# Revit family: 820-20-028-DN150-1600
name_source: partatom
category: Generic Models
units: mm (PartAtom-declared; Revit-internal decimal feet)

## family parameters
Always vertical = Yes
Can host rebar = No
Cut with Voids When Loaded = No
Part Type = Normal
Room Calculation Point = No
Round Connector Dimension = Use Diameter
Shared = No
Work Plane-Based = No

## types (33) — shared parameters
820-0150-20-041E0160002 = DN150_PN 10/16
820-0200-20-041E0030002 = DN200_PN10
820-0200-20-041E0160002 = DN200_PN16
820-0250-20-041E0030002 = DN250_PN10
820-0250-20-041E0160002 = DN250_PN16
820-0300-20-041E0030002 = DN300_PN10
820-0300-20-041E0160002 = DN300_PN16
820-0350-20-04010030002 = DN350_PN10
820-0350-20-04010160002 = DN350_PN16
820-0400-20-04010030002 = DN400_PN10
820-0400-20-04010160002 = DN400_PN16
820-0450-20-04040031002 = DN450_PN10
820-0450-20-04040161002 = DN450_PN16
820-0500-20-04040031002 = DN500_PN10
820-0500-20-04040161002 = DN500_PN16
820-0600-20-04040031002 = DN600_PN10
820-0600-20-04040161002 = DN600_PN16
820-0700-20-04040031002 = DN700_PN10
820-0700-20-04040161002 = DN700_PN16
820-0800-20-04040031002 = DN800_PN10
820-0800-20-04040161002 = DN800_PN16
820-0900-20-04040031002 = DN900_PN10
820-0900-20-04040161002 = DN900_PN16
820-1000-20-04040031002 = DN1000_PN10
820-1000-20-04040161002 = DN1000_PN16
820-1100-20-04040031002 = DN1100_PN10
820-1100-20-04040161002 = DN1100_PN16
820-1200-20-04040031002 = DN1200_PN10
820-1200-20-04040161002 = DN1200_PN16
820-1400-20-04040031002 = DN1400_PN10
820-1400-20-04040161002 = DN1400_PN16
820-1600-20-04040031002 = DN1600_PN10
820-1600-20-04040161002 = DN1600_PN16
Body_wallthickness = 10 mm  [stored 0.0328084 ft]
Description_ = AVK CENTRIC U-SECTION BUTTERFLY VALVE
Search_table = 820-20-028-DN150-1600
URL product pages = https://www.avkvalves.com

## per-type parameters (varying)
| type | DN | F | F2 | Flange_thickness | H2 | ID | L | L2 | L_ref | L_ref_2 | L_ref_3 | W2_ref |
| DN0150_PN10/16 | 150 mm | 14 mm  [stored 0.0459318 ft] | 16 mm  [stored 0.0524934 ft] | 10 mm  [stored 0.0328084 ft] | 143 mm | 75 mm | 56 mm  [stored 0.183727 ft] | 143 mm | 36 mm  [stored 0.11811 ft] | 54 mm  [stored 0.177165 ft] | 30 mm  [stored 0.0984252 ft] | 210 mm |
| DN0200_PN10 | 200 mm | 17 mm  [stored 0.0557743 ft] | 19 mm  [stored 0.062336 ft] | 10 mm  [stored 0.0328084 ft] | 170 mm | 100 mm  [stored 0.328084 ft] | 60 mm  [stored 0.19685 ft] | 170 mm | 40 mm  [stored 0.131234 ft] | 60 mm  [stored 0.19685 ft] | 33 mm | 240 mm |
| DN0200_PN16 | 200 mm | 17 mm  [stored 0.0557743 ft] | 19 mm  [stored 0.062336 ft] | 10 mm  [stored 0.0328084 ft] | 170 mm | 100 mm  [stored 0.328084 ft] | 60 mm  [stored 0.19685 ft] | 170 mm | 40 mm  [stored 0.131234 ft] | 60 mm  [stored 0.19685 ft] | 33 mm | 240 mm |
| DN0250_PN10 | 250 mm | 22 mm  [stored 0.0721785 ft] | 24 mm  [stored 0.0787402 ft] | 10 mm  [stored 0.0328084 ft] | 200 mm | 125 mm | 68 mm  [stored 0.223097 ft] | 203 mm | 48 mm  [stored 0.15748 ft] | 72 mm  [stored 0.23622 ft] | 40 mm  [stored 0.131234 ft] | 279 mm |
| DN0250_PN16 | 250 mm | 22 mm  [stored 0.0721785 ft] | 24 mm  [stored 0.0787402 ft] | 10 mm  [stored 0.0328084 ft] | 200 mm | 125 mm | 68 mm  [stored 0.223097 ft] | 203 mm | 48 mm  [stored 0.15748 ft] | 72 mm  [stored 0.23622 ft] | 40 mm  [stored 0.131234 ft] | 279 mm |
| DN0300_PN10 | 300 mm | 22 mm  [stored 0.0721785 ft] | 24 mm  [stored 0.0787402 ft] | 10 mm  [stored 0.0328084 ft] | 239 mm | 150 mm | 78 mm  [stored 0.255906 ft] | 241 mm | 58 mm  [stored 0.190289 ft] | 87 mm  [stored 0.285433 ft] | 48 mm  [stored 0.15748 ft] | 315 mm |
| DN0300_PN16 | 300 mm | 22 mm  [stored 0.0721785 ft] | 24 mm  [stored 0.0787402 ft] | 10 mm  [stored 0.0328084 ft] | 239 mm | 150 mm | 78 mm  [stored 0.255906 ft] | 241 mm | 58 mm  [stored 0.190289 ft] | 87 mm  [stored 0.285433 ft] | 48 mm  [stored 0.15748 ft] | 315 mm |
| DN0350_PN10 | 350 mm | 22 mm  [stored 0.0721785 ft] | 40 mm  [stored 0.131234 ft] | 12 mm  [stored 0.0393701 ft] | 265 mm | 175 mm | 80 mm  [stored 0.262467 ft] | 267 mm | 56 mm  [stored 0.183727 ft] | 84 mm  [stored 0.275591 ft] | 47 mm | 330 mm |
| DN0350_PN16 | 350 mm | 22 mm  [stored 0.0721785 ft] | 40 mm  [stored 0.131234 ft] | 12 mm  [stored 0.0393701 ft] | 265 mm | 175 mm | 80 mm  [stored 0.262467 ft] | 267 mm | 56 mm  [stored 0.183727 ft] | 84 mm  [stored 0.275591 ft] | 47 mm | 330 mm |
| DN0400_PN10 | 400 mm | 27 mm  [stored 0.0885827 ft] | 40 mm  [stored 0.131234 ft] | 12 mm  [stored 0.0393701 ft] | 296 mm | 200 mm | 102 mm | 299 mm | 78 mm  [stored 0.255906 ft] | 117 mm | 65 mm  [stored 0.213255 ft] | 365 mm |
| DN0400_PN16 | 400 mm | 27 mm  [stored 0.0885827 ft] | 40 mm  [stored 0.131234 ft] | 12 mm  [stored 0.0393701 ft] | 296 mm | 200 mm | 102 mm | 299 mm | 78 mm  [stored 0.255906 ft] | 117 mm | 65 mm  [stored 0.213255 ft] | 365 mm |
| DN0450_PN10 | 450 mm | 45 mm  [stored 0.147638 ft] | 65 mm  [stored 0.213255 ft] | 15 mm  [stored 0.0492126 ft] | 355 mm | 225 mm | 113 mm | 320 mm | 83 mm  [stored 0.27231 ft] | 125 mm | 69 mm  [stored 0.226378 ft] | 397 mm |
| DN0450_PN16 | 450 mm | 45 mm  [stored 0.147638 ft] | 65 mm  [stored 0.213255 ft] | 15 mm  [stored 0.0492126 ft] | 355 mm | 225 mm | 113 mm | 320 mm | 83 mm  [stored 0.27231 ft] | 125 mm | 69 mm  [stored 0.226378 ft] | 397 mm |
| DN0500_PN10 | 500 mm | 45 mm  [stored 0.147638 ft] | 65 mm  [stored 0.213255 ft] | 17 mm  [stored 0.0557743 ft] | 393 mm | 250 mm | 126 mm | 358 mm | 92 mm  [stored 0.301837 ft] | 138 mm | 77 mm | 437 mm |
| DN0500_PN16 | 500 mm | 45 mm  [stored 0.147638 ft] | 65 mm  [stored 0.213255 ft] | 17 mm  [stored 0.0557743 ft] | 393 mm | 250 mm | 126 mm | 358 mm | 92 mm  [stored 0.301837 ft] | 138 mm | 77 mm | 437 mm |
| DN0600_PN10 | 600 mm | 70 mm  [stored 0.229659 ft] | 80 mm  [stored 0.262467 ft] | 17 mm  [stored 0.0557743 ft] | 464 mm | 300 mm | 153 mm | 420 mm | 119 mm | 179 mm | 99 mm | 522 mm |
| DN0600_PN16 | 600 mm | 70 mm  [stored 0.229659 ft] | 80 mm  [stored 0.262467 ft] | 17 mm  [stored 0.0557743 ft] | 464 mm | 300 mm | 153 mm | 420 mm | 119 mm | 179 mm | 99 mm | 522 mm |
| DN0700_PN10 | 700 mm | 70 mm  [stored 0.229659 ft] | 80 mm  [stored 0.262467 ft] | 19 mm  [stored 0.062336 ft] | 503 mm | 350 mm | 168 mm | 464 mm | 130 mm | 195 mm | 108 mm | 565 mm |
| DN0700_PN16 | 700 mm | 70 mm  [stored 0.229659 ft] | 80 mm  [stored 0.262467 ft] | 19 mm  [stored 0.062336 ft] | 503 mm | 350 mm | 168 mm | 464 mm | 130 mm | 195 mm | 108 mm | 565 mm |
| DN0800_PN10 | 800 mm | 70 mm  [stored 0.229659 ft] | 80 mm  [stored 0.262467 ft] | 21 mm  [stored 0.0688976 ft] | 577 mm | 400 mm | 190 mm | 530 mm | 148 mm | 222 mm | 123 mm | 627 mm |
| DN0800_PN16 | 800 mm | 70 mm  [stored 0.229659 ft] | 80 mm  [stored 0.262467 ft] | 21 mm  [stored 0.0688976 ft] | 577 mm | 400 mm | 190 mm | 530 mm | 148 mm | 222 mm | 123 mm | 627 mm |
| DN0900_PN10 | 900 mm | 80 mm  [stored 0.262467 ft] | 100 mm  [stored 0.328084 ft] | 23 mm  [stored 0.0754593 ft] | 643 mm | 450 mm | 204 mm | 585 mm | 158 mm | 237 mm | 132 mm | 696 mm |
| DN0900_PN16 | 900 mm | 80 mm  [stored 0.262467 ft] | 100 mm  [stored 0.328084 ft] | 23 mm  [stored 0.0754593 ft] | 643 mm | 450 mm | 204 mm | 585 mm | 158 mm | 237 mm | 132 mm | 696 mm |
| DN1000_PN10 | 1000 mm | 80 mm  [stored 0.262467 ft] | 100 mm  [stored 0.328084 ft] | 25 mm  [stored 0.082021 ft] | 693 mm | 500 mm | 218 mm | 628 mm | 168 mm | 252 mm | 140 mm | 745 mm |
| DN1000_PN16 | 1000 mm | 80 mm  [stored 0.262467 ft] | 100 mm  [stored 0.328084 ft] | 25 mm  [stored 0.082021 ft] | 693 mm | 500 mm | 218 mm | 628 mm | 168 mm | 252 mm | 140 mm | 745 mm |
| DN1100_PN10 | 1100 mm | 80 mm  [stored 0.262467 ft] | 100 mm  [stored 0.328084 ft] | 25 mm  [stored 0.082021 ft] | 738 mm | 550 mm | 218 mm | 698 mm | 168 mm | 252 mm | 140 mm | 820 mm |
| DN1100_PN16 | 1100 mm | 80 mm  [stored 0.262467 ft] | 100 mm  [stored 0.328084 ft] | 25 mm  [stored 0.082021 ft] | 738 mm | 550 mm | 218 mm | 698 mm | 168 mm | 252 mm | 140 mm | 820 mm |
| DN1200_PN10 | 1200 mm | 100 mm  [stored 0.328084 ft] | 120 mm | 27 mm  [stored 0.0885827 ft] | 806 mm | 600 mm | 254 mm | 743 mm | 200 mm | 300 mm | 167 mm | 881 mm |
| DN1200_PN16 | 1200 mm | 100 mm  [stored 0.328084 ft] | 120 mm | 27 mm  [stored 0.0885827 ft] | 806 mm | 600 mm | 254 mm | 743 mm | 200 mm | 300 mm | 167 mm | 881 mm |
| DN1400_PN10 | 1400 mm | 120 mm | 120 mm | 29 mm  [stored 0.0951444 ft] | 908 mm | 700 mm | 280 mm | 873 mm | 222 mm | 333 mm | 185 mm | 990 mm |
| DN1400_PN16 | 1400 mm | 120 mm | 120 mm | 29 mm  [stored 0.0951444 ft] | 908 mm | 700 mm | 280 mm | 873 mm | 222 mm | 333 mm | 185 mm | 990 mm |
| DN1600_PN10 | 1600 mm | 130 mm | 155 mm | 29 mm  [stored 0.0951444 ft] | 1048 mm | 800 mm | 318 mm | 962 mm | 260 mm | 390 mm | 217 mm | 1117 mm |
| DN1600_PN16 | 1600 mm | 130 mm | 155 mm | 29 mm  [stored 0.0951444 ft] | 1048 mm | 800 mm | 318 mm | 962 mm | 260 mm | 390 mm | 217 mm | 1117 mm |

note: [stored X ft] marks values corroborated as IEEE doubles in the binary element streams (Revit-internal decimal feet)

## geometry (parser evidence)
native form markers: Sweep x5
no freeform markers — native parametric forms only
